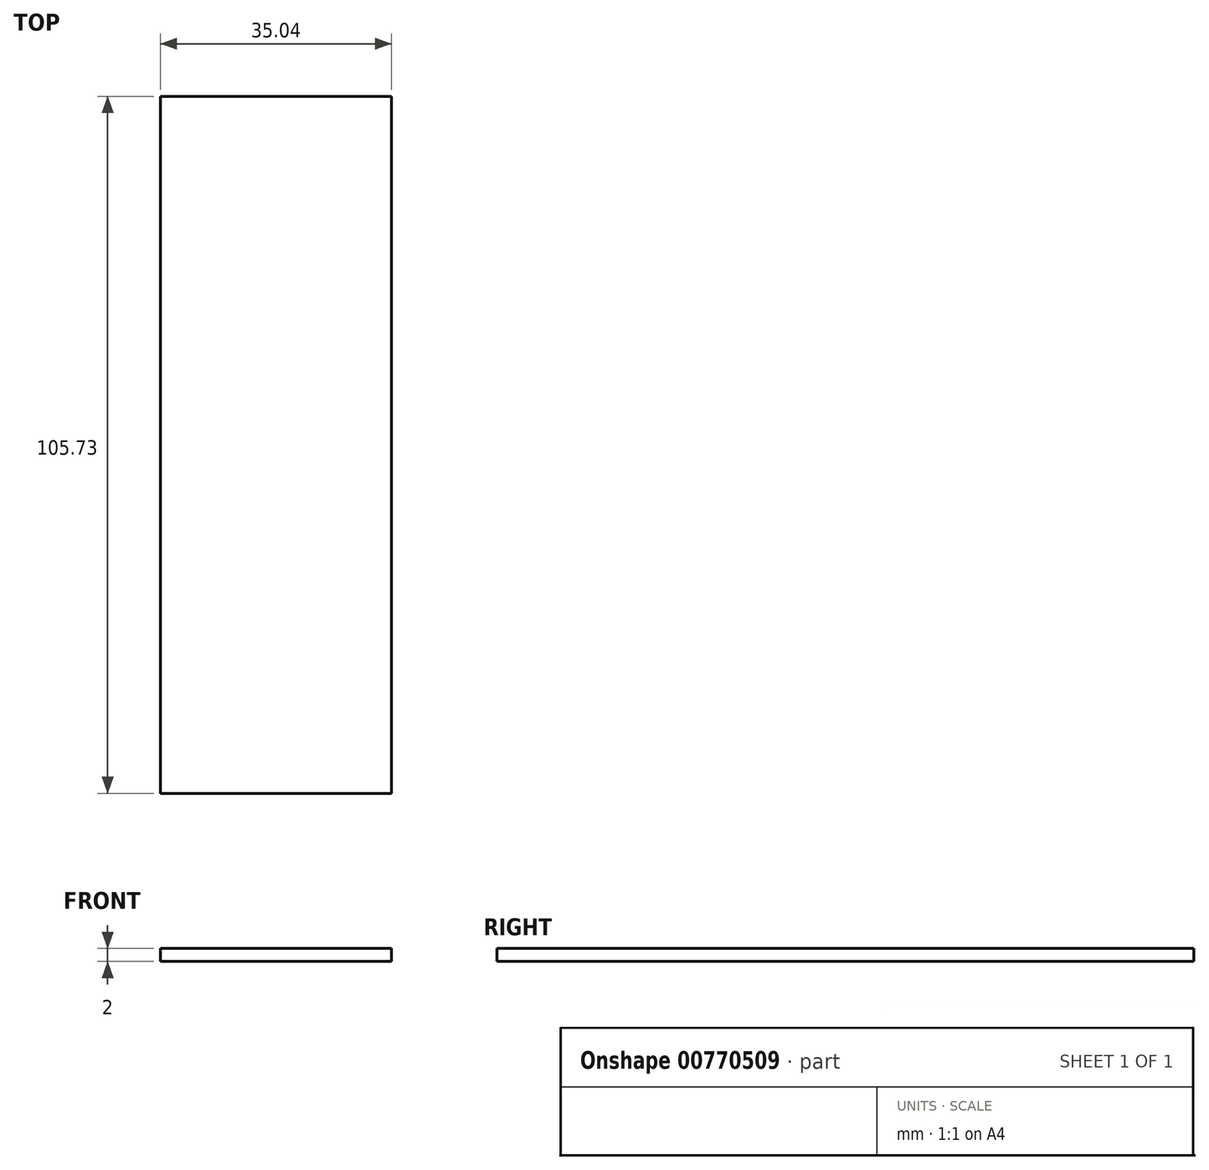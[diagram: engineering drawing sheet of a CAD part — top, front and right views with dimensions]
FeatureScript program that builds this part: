
annotation { "Feature Type Name" : "Feature", "Feature Type Description" : "" }
export const myFeature = defineFeature(function(context is Context, id is Id, definition is map)
    precondition{}
    {
        {
            var Q0;
            Q0=qCreatedBy(makeId("Top.planeOp"),FACE);
            var sketch = newSketch(context, id + "F0", { "sketchPlane" : qUnion([Q0])});
            skLineSegment(sketch, "E0.bottom", {"start": v(-58.24, -56.02) * mm, "end": v(-23.2, -56.02) * mm});
            skLineSegment(sketch, "E0.top", {"start": v(-58.24, 49.7) * mm, "end": v(-23.2, 49.7) * mm});
            skLineSegment(sketch, "E0.left", {"start": v(-58.24, -56.02) * mm, "end": v(-58.24, 49.7) * mm});
            skLineSegment(sketch, "E0.right", {"start": v(-23.2, -56.02) * mm, "end": v(-23.2, 49.7) * mm});
            skSolve(sketch);
        }
        {
            var Q0;
            Q0=makeQuery(id+"F0.imprint","IMPRINT",FACE,{"disambiguationData":[TD([[makeQuery(id+"F0.imprint","IMPRINT",EDGE,{"derivedFrom":sQuery(id+"F0.wireOp",EDGE,"E0.bottom")}),1.0]])]});
            extrude(context, id + "F1", {"entities" : qUnion([Q0]), "depth" : 2 * mm, "offsetDistance" : 25 * mm});
        }
    });
